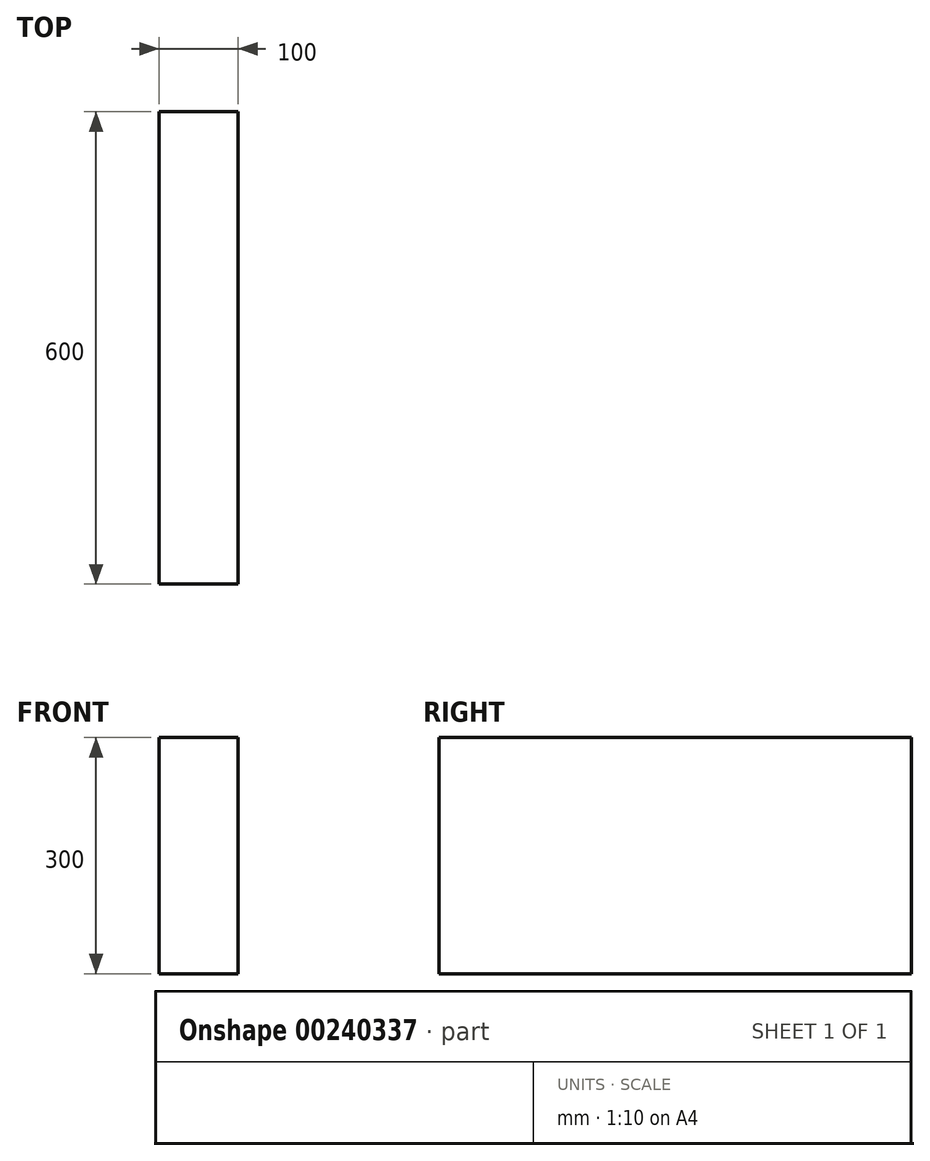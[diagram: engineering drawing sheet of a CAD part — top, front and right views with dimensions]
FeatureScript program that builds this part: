
annotation { "Feature Type Name" : "Feature", "Feature Type Description" : "" }
export const myFeature = defineFeature(function(context is Context, id is Id, definition is map)
    precondition{}
    {
        {
            var Q0;
            Q0=qCreatedBy(makeId("Right.planeOp"),FACE);
            var sketch = newSketch(context, id + "F0", { "sketchPlane" : qUnion([Q0])});
            skLineSegment(sketch, "E0.bottom", {"start": v(300, 150) * mm, "end": v(-300, 150) * mm});
            skLineSegment(sketch, "E0.top", {"start": v(300, -150) * mm, "end": v(-300, -150) * mm});
            skLineSegment(sketch, "E0.left", {"start": v(300, 150) * mm, "end": v(300, -150) * mm});
            skLineSegment(sketch, "E0.right", {"start": v(-300, 150) * mm, "end": v(-300, -150) * mm});
            skPoint(sketch, "E0.middle", {"position": v(0, 0) * mm});
            skSolve(sketch);
        }
        {
            var Q0;
            Q0=qSketchRegion(id+"F0",true);
            extrude(context, id + "F1", {"entities" : qUnion([Q0]), "endBound" : BoundingType.SYMMETRIC, "depth" : 100 * mm});
        }
    });
